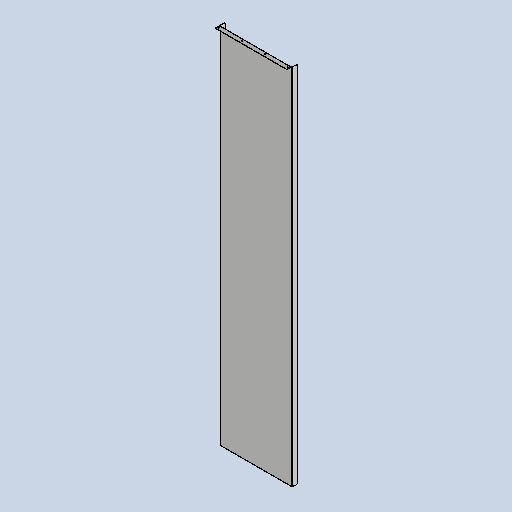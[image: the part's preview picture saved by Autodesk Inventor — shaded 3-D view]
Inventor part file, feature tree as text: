
AUTODESK INVENTOR PART (.ipt)
format: ipt  version: 2025 (Build 290162010, 162A)  size: 178,176 bytes
history: native  units: mm
features: sheet_metal_op x7, sketch x7, other x5, extrude x4, reference x4, projected_geometry x2, mirror x1
ambient origin geometry x8: Origin, YZ Plane, XZ Plane, XY Plane, X Axis, Y Axis, Z Axis, Center Point
bodies: Solid1 (feature_tree)
feature tree (30):
  sheet_metal_op  "Face1"
  sheet_metal_op  "Flange1"
  sheet_metal_op  "Flange2"
  extrude  "Extrusion1"  Depth=400.0mm
  extrude  "Extrusion2"  Depth=2.0mm
  extrude  "Extrusion3"  Depth=4.0mm
  extrude  "Extrusion4"  Depth=30.0mm TaperAngle=90.0deg
  mirror  "Mirror1"
  sketch  "Sketch1"  dims[d0=2011.081mm d1=400.0mm]
  other  "Plate1"
  sketch  "Sketch2"  dims[d2=2.0mm d3=2.0mm]
  other  "Plate2"
  sheet_metal_op  "Bend1"
  sheet_metal_op  "Corner1"
  sketch  "Sketch3"  dims[d4=1.0mm d5=4.0mm]
  projected_geometry  "Projected Loop1"
  sketch  "Sketch4"  dims[d6=2.75mm d7=30.0mm d8=90.0deg d9=2.75mm]
  other  "Plate3"
  sheet_metal_op  "Bend2"
  sheet_metal_op  "Corner2"
  sketch  "Sketch5"  dims[d10=8.0mm]
  sketch  "Sketch6"  dims[d11=2.0mm]
  reference  "Reference1"
  reference  "Reference2"
  reference  "Reference3"
  reference  "Reference4"
  sketch  "Sketch7"  dims[d12=2.75mm d13=1.001819mm d14=0.0mm d15=0.0mm d16=2.0mm d17=1.0mm d18=4.0mm d19=2.75mm d20=30.0mm d21=14.706144mm d22=2.75mm d23=8.0mm d24=2.0mm d25=2.75mm d26=1.001819mm d27=0.0mm d28=0.0mm d29=10.0mm d30=0.0mm d31=2.0mm d32=0.0mm]
  projected_geometry  "Projected Loop2"
  other  "ASY MSC 001 отстойник осветлитель.iam"
  other  "MSC 073 ridge 3.ipt:1"
